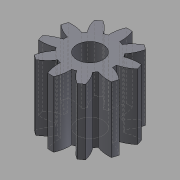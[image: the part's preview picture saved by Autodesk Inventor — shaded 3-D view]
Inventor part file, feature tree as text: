
AUTODESK INVENTOR PART (.ipt)
format: ipt  version: 2015 (Build 190159000, 159)  size: 182,784 bytes
history: native  units: in
note: dims shown in document units (in); Inventor stores cm internally (conversion verified against a paired STEP export)
features: other x13, sketch x3, plane x2
ambient origin geometry x8: Origin, YZ Plane, XZ Plane, XY Plane, X Axis, Y Axis, Z Axis, Center Point
bodies: Solid1 (feature_tree)
feature tree (18):
  other  "Spur Gear1"
  other  "Solid1::Spur Gear1"
  other  "TaggingFeature1"
  sketch  "Sketch1"  dims[d0=0.3937in]
  sketch  "Sketch2"  dims[d16=0.4724in d17=0.0in d41=0.0in d43=0.4724in d46=0.4724in d47=0.0in d48=0.0in]
  sketch  "Sketch3"
  plane  "XZ Plane_1"
  plane  "Work Plane2"
  other  "Z Axis_1"
  other  "Srf1"
  other  "Srf1::Derived"
  other  "Distance iMate"
  other  "Align iMate"
  other  "Mesh iMate"
  other  "Axis iMate"
  other  "Position iMate"
  other  "Mesh iMate2"
  other  "Start plane iMate"
